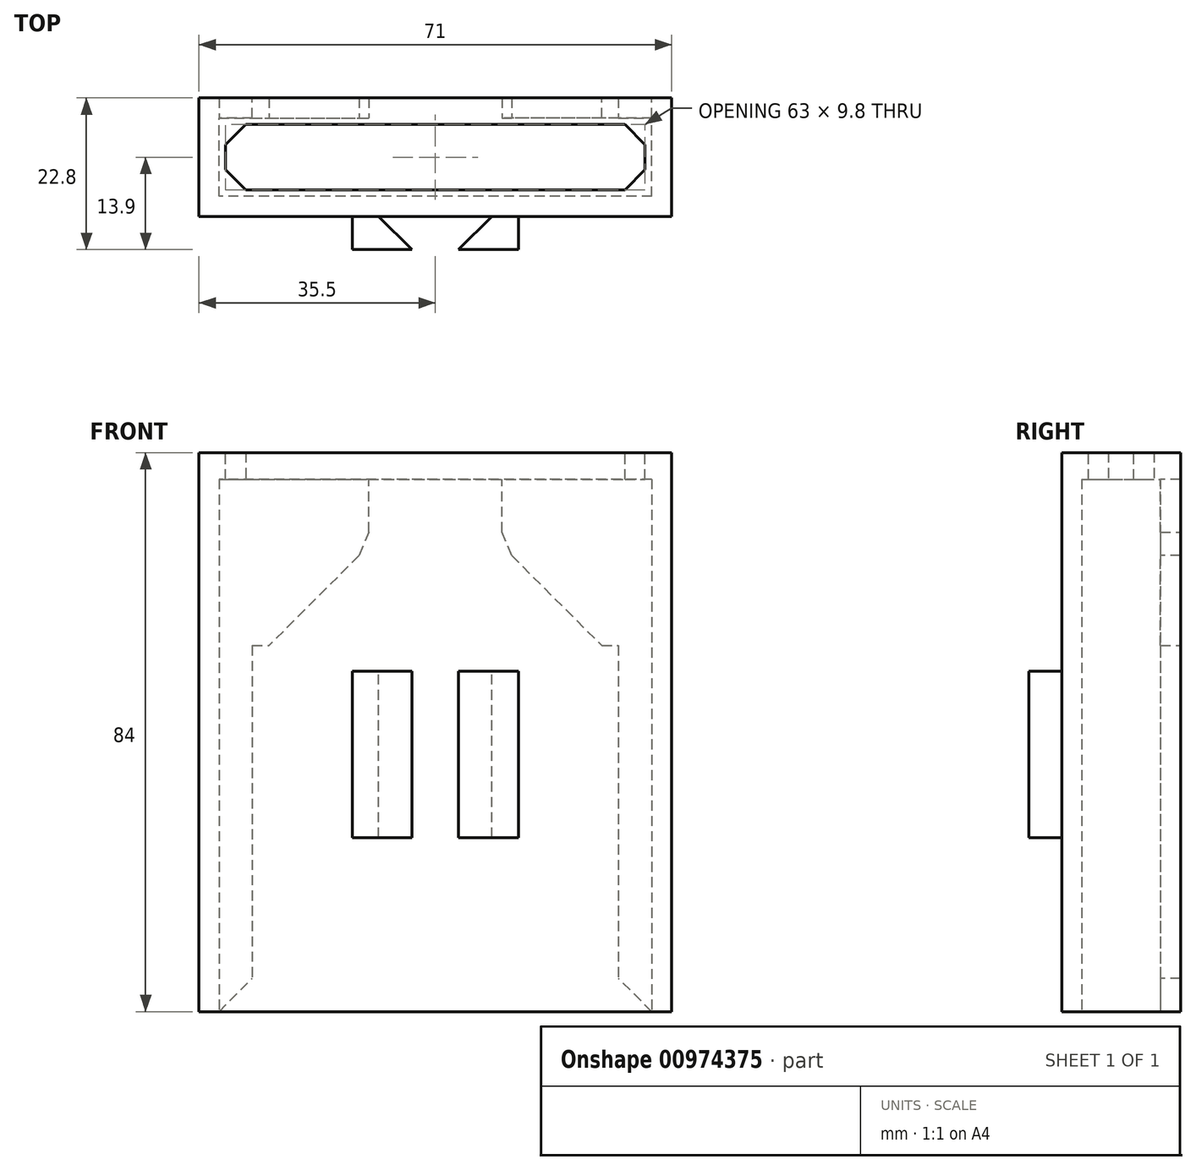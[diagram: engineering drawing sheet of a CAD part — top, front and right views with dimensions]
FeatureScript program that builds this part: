
annotation { "Feature Type Name" : "Feature", "Feature Type Description" : "" }
export const myFeature = defineFeature(function(context is Context, id is Id, definition is map)
    precondition{}
    {
        {
            var Q0;
            Q0=qCreatedBy(makeId("Top.planeOp"),FACE);
            var sketch = newSketch(context, id + "F0", { "sketchPlane" : qUnion([Q0])});
            skLineSegment(sketch, "E0.bottom", {"start": v(0, 0) * mm, "end": v(-32.5, 0) * mm});
            skLineSegment(sketch, "E0.top", {"start": v(0, 3) * mm, "end": v(-32.5, 3) * mm});
            skLineSegment(sketch, "E0.left", {"start": v(0, 0) * mm, "end": v(0, 3) * mm});
            skLineSegment(sketch, "E0.right", {"start": v(-32.5, 0) * mm, "end": v(-32.5, 3) * mm});
            skLineSegment(sketch, "E1.bottom", {"start": v(-32.5, 0) * mm, "end": v(-35.5, 0) * mm});
            skLineSegment(sketch, "E1.top", {"start": v(-32.5, 14.8) * mm, "end": v(-35.5, 14.8) * mm});
            skLineSegment(sketch, "E1.left", {"start": v(-32.5, 0) * mm, "end": v(-32.5, 14.8) * mm});
            skLineSegment(sketch, "E1.right", {"start": v(-35.5, 0) * mm, "end": v(-35.5, 14.8) * mm});
            skLineSegment(sketch, "E2.bottom", {"start": v(-35.5, 14.8) * mm, "end": v(-27.5, 14.8) * mm});
            skLineSegment(sketch, "E2.top", {"start": v(-35.5, 17.8) * mm, "end": v(-27.5, 17.8) * mm});
            skLineSegment(sketch, "E2.left", {"start": v(-35.5, 14.8) * mm, "end": v(-35.5, 17.8) * mm});
            skLineSegment(sketch, "E2.right", {"start": v(-27.5, 14.8) * mm, "end": v(-27.5, 17.8) * mm});
            skLineSegment(sketch, "E3.MirrorCS", {"start": v(0, 0) * mm, "end": v(32.5, 0) * mm});
            skLineSegment(sketch, "E4.MirrorCS", {"start": v(32.5, 0) * mm, "end": v(32.5, 14.8) * mm});
            skLineSegment(sketch, "E5.MirrorCS", {"start": v(35.5, 14.8) * mm, "end": v(35.5, 17.8) * mm});
            skLineSegment(sketch, "E6.MirrorCS", {"start": v(35.5, 0) * mm, "end": v(35.5, 14.8) * mm});
            skLineSegment(sketch, "E7.MirrorCS", {"start": v(0, 3) * mm, "end": v(32.5, 3) * mm});
            skLineSegment(sketch, "E8.MirrorCS", {"start": v(27.5, 14.8) * mm, "end": v(27.5, 17.8) * mm});
            skLineSegment(sketch, "E9.MirrorCS", {"start": v(32.5, 0) * mm, "end": v(32.5, 3) * mm});
            skLineSegment(sketch, "E10.MirrorCS", {"start": v(35.5, 14.8) * mm, "end": v(27.5, 14.8) * mm});
            skLineSegment(sketch, "E11.MirrorCS", {"start": v(32.5, 0) * mm, "end": v(35.5, 0) * mm});
            skLineSegment(sketch, "E12.MirrorCS", {"start": v(35.5, 17.8) * mm, "end": v(27.5, 17.8) * mm});
            skLineSegment(sketch, "E13.MirrorCS", {"start": v(32.5, 14.8) * mm, "end": v(35.5, 14.8) * mm});
            skSolve(sketch);
        }
        {
            var Q0;
            {var subQ5=sQuery(id+"F0.wireOp",EDGE,"E1.bottom");Q0=makeQuery(id+"F0.imprint","IMPRINT",FACE,{"disambiguationData":[TD([[makeQuery(id+"F0.imprint","IMPRINT",EDGE,{"derivedFrom":subQ5}),-1.0]])]});}
            var Q1;
            Q1=makeQuery(id+"F0.imprint","IMPRINT",FACE,{"disambiguationData":[TD([[makeQuery(id+"F0.imprint","IMPRINT",EDGE,{"derivedFrom":sQuery(id+"F0.wireOp",EDGE,"E4.MirrorCS")}),-1.0]])]});
            var Q2;
            {var subQ0=sQuery(id+"F0.wireOp",EDGE,"E0.bottom");Q2=makeQuery(id+"F0.imprint","IMPRINT",FACE,{"disambiguationData":[TD([[makeQuery(id+"F0.imprint","IMPRINT",EDGE,{"derivedFrom":subQ0}),-1.0]])]});}
            var Q3;
            Q3=makeQuery(id+"F0.imprint","IMPRINT",FACE,{"disambiguationData":[TD([[makeQuery(id+"F0.imprint","IMPRINT",EDGE,{"derivedFrom":sQuery(id+"F0.wireOp",EDGE,"E3.MirrorCS")}),1.0]])]});
            var Q4;
            Q4=makeQuery(id+"F0.imprint","IMPRINT",FACE,{"disambiguationData":[TD([[makeQuery(id+"F0.imprint","IMPRINT",EDGE,{"derivedFrom":sQuery(id+"F0.wireOp",EDGE,"E2.top")}),-1.0]])]});
            var Q5;
            Q5=makeQuery(id+"F0.imprint","IMPRINT",FACE,{"disambiguationData":[TD([[makeQuery(id+"F0.imprint","IMPRINT",EDGE,{"derivedFrom":sQuery(id+"F0.wireOp",EDGE,"E5.MirrorCS")}),1.0]])]});
            extrude(context, id + "F1", {"entities" : qUnion([Q0, Q1, Q2, Q3, Q4, Q5]), "depth" : 80 * mm, "offsetDistance" : 25 * mm});
        }
        {
            var Q0;
            Q0=makeQuery(id+"F1.opExtrude","CAP_FACE",FACE,{"disambiguationData":[OSD([sQuery(id+"F0.wireOp",EDGE,"E0.bottom"),sQuery(id+"F0.wireOp",EDGE,"E0.top"),sQuery(id+"F0.wireOp",EDGE,"E1.bottom"),sQuery(id+"F0.wireOp",EDGE,"E1.left"),sQuery(id+"F0.wireOp",EDGE,"E1.right"),sQuery(id+"F0.wireOp",EDGE,"E2.bottom"),sQuery(id+"F0.wireOp",EDGE,"E2.top"),sQuery(id+"F0.wireOp",EDGE,"E2.left"),sQuery(id+"F0.wireOp",EDGE,"E2.right"),sQuery(id+"F0.wireOp",EDGE,"E3.MirrorCS"),sQuery(id+"F0.wireOp",EDGE,"E4.MirrorCS"),sQuery(id+"F0.wireOp",EDGE,"E5.MirrorCS"),sQuery(id+"F0.wireOp",EDGE,"E6.MirrorCS"),sQuery(id+"F0.wireOp",EDGE,"E7.MirrorCS"),sQuery(id+"F0.wireOp",EDGE,"E8.MirrorCS"),sQuery(id+"F0.wireOp",EDGE,"E10.MirrorCS"),sQuery(id+"F0.wireOp",EDGE,"E11.MirrorCS"),sQuery(id+"F0.wireOp",EDGE,"E12.MirrorCS")])],"isStart":false});
            var sketch = newSketch(context, id + "F2", { "sketchPlane" : qUnion([Q0])});
            skLineSegment(sketch, "E14.bottom", {"start": v(-35.5, 17.8) * mm, "end": v(35.5, 17.8) * mm});
            skLineSegment(sketch, "E14.top", {"start": v(-35.5, 0) * mm, "end": v(35.5, 0) * mm});
            skLineSegment(sketch, "E14.left", {"start": v(-35.5, 17.8) * mm, "end": v(-35.5, 0) * mm});
            skLineSegment(sketch, "E14.right", {"start": v(35.5, 17.8) * mm, "end": v(35.5, 0) * mm});
            skSolve(sketch);
        }
        {
            var Q0;
            Q0=makeQuery(id+"F2.imprint","IMPRINT",FACE,{"disambiguationData":[TD([[makeQuery(id+"F2.imprint","IMPRINT",EDGE,{"derivedFrom":makeQuery(id+"F1.opExtrude","CAP_EDGE",EDGE,{"disambiguationData":[OSD([sQuery(id+"F0.wireOp",EDGE,"E1.left")])],"isStart":false})}),-1.0]])]});
            var Q1;
            Q1=makeQuery(id+"F2.imprint","IMPRINT",FACE,{"disambiguationData":[TD([[makeQuery(id+"F2.imprint","IMPRINT",EDGE,{"derivedFrom":sQuery(id+"F2.wireOp",EDGE,"E14.top")}),-1.0]])]});
            extrude(context, id + "F3", {"entities" : qUnion([Q0, Q1]), "operationType" : NewBodyOperationType.ADD, "depth" : 4 * mm, "offsetDistance" : 25 * mm});
        }
        {
            var Q0;
            Q0=makeQuery(id+"F3.opExtrude","CAP_FACE",FACE,{"disambiguationData":[OSD([sQuery(id+"F2.wireOp",EDGE,"E14.bottom"),sQuery(id+"F2.wireOp",EDGE,"E14.top"),sQuery(id+"F2.wireOp",EDGE,"E14.left"),sQuery(id+"F2.wireOp",EDGE,"E14.right")])],"isStart":true});
            var sketch = newSketch(context, id + "F4", { "sketchPlane" : qUnion([Q0])});
            skLineSegment(sketch, "E15.bottom", {"start": v(-27.5, -17.8) * mm, "end": v(-10, -17.8) * mm});
            skLineSegment(sketch, "E15.top", {"start": v(-27.5, -14.8) * mm, "end": v(-10, -14.8) * mm});
            skLineSegment(sketch, "E15.left", {"start": v(-27.5, -17.8) * mm, "end": v(-27.5, -14.8) * mm});
            skLineSegment(sketch, "E15.right", {"start": v(-10, -17.8) * mm, "end": v(-10, -14.8) * mm});
            skPoint(sketch, "E16.MirrorCS.end.orphan", {"position": v(-10, -11.8) * mm});
            skPoint(sketch, "E16.MirrorCS.start.orphan", {"position": v(-27.5, -11.8) * mm});
            skPoint(sketch, "E17.MirrorCS.end.orphan", {"position": v(-10, -14.8) * mm});
            skPoint(sketch, "E18.MirrorCS.end.orphan", {"position": v(-27.5, -14.8) * mm});
            skLineSegment(sketch, "E19.MirrorCS", {"start": v(27.5, -17.8) * mm, "end": v(10, -17.8) * mm});
            skLineSegment(sketch, "E20.MirrorCS", {"start": v(10, -17.8) * mm, "end": v(10, -14.8) * mm});
            skLineSegment(sketch, "E21.MirrorCS", {"start": v(27.5, -14.8) * mm, "end": v(10, -14.8) * mm});
            skLineSegment(sketch, "E22.MirrorCS", {"start": v(27.5, -17.8) * mm, "end": v(27.5, -14.8) * mm});
            skSolve(sketch);
        }
        {
            var Q0;
            Q0=makeQuery(id+"F4.imprint","IMPRINT",FACE,{"disambiguationData":[TD([[makeQuery(id+"F4.imprint","IMPRINT",EDGE,{"derivedFrom":sQuery(id+"F4.wireOp",EDGE,"E15.bottom")}),1.0]])]});
            var Q1;
            Q1=makeQuery(id+"F4.imprint","IMPRINT",FACE,{"disambiguationData":[TD([[makeQuery(id+"F4.imprint","IMPRINT",EDGE,{"derivedFrom":sQuery(id+"F4.wireOp",EDGE,"E19.MirrorCS")}),1.0]])]});
            extrude(context, id + "F5", {"entities" : qUnion([Q0, Q1]), "operationType" : NewBodyOperationType.ADD, "depth" : 25 * mm, "offsetDistance" : 25 * mm});
        }
        {
            var Q0;
            Q0=makeQuery(id+"F5.opExtrude","CAP_EDGE",EDGE,{"disambiguationData":[OSD([sQuery(id+"F4.wireOp",EDGE,"E15.right")])],"isStart":false});
            var Q1;
            Q1=makeQuery(id+"F5.opExtrude","CAP_EDGE",EDGE,{"disambiguationData":[OSD([sQuery(id+"F4.wireOp",EDGE,"E20.MirrorCS")])],"isStart":false});
            chamfer(context, id + "F6", {"entities" : qUnion([Q0, Q1]), "width" : 15 * mm, "tangentPropagation" : true});
        }
        {
            var Q0;
            {var subQ0=sQuery(id+"F4.wireOp",EDGE,"E15.right");Q0=makeQuery(id+"F6.opChamfer","BLEND_EDGE",EDGE,{"blendedFrom":[makeQuery(id+"F5.opExtrude","CAP_EDGE",EDGE,{"disambiguationData":[OSD([subQ0])],"isStart":false}),makeQuery(id+"F5.opExtrude","SWEPT_FACE",FACE,{"disambiguationData":[OSD([subQ0])]})],"blendedInto":[makeQuery(id+"F5.opExtrude","SWEPT_FACE",FACE,{"disambiguationData":[OSD([subQ0])]})]});}
            var Q1;
            {var subQ0=sQuery(id+"F4.wireOp",EDGE,"E20.MirrorCS");Q1=makeQuery(id+"F6.opChamfer","BLEND_EDGE",EDGE,{"blendedFrom":[makeQuery(id+"F5.opExtrude","CAP_EDGE",EDGE,{"disambiguationData":[OSD([subQ0])],"isStart":false}),makeQuery(id+"F5.opExtrude","SWEPT_FACE",FACE,{"disambiguationData":[OSD([subQ0])]})],"blendedInto":[makeQuery(id+"F5.opExtrude","SWEPT_FACE",FACE,{"disambiguationData":[OSD([subQ0])]})]});}
            chamfer(context, id + "F7", {"entities" : qUnion([Q0, Q1]), "width" : 5 * mm, "tangentPropagation" : true});
        }
        {
            var Q0;
            Q0=makeQuery(id+"F3.opExtrude","CAP_FACE",FACE,{"disambiguationData":[OSD([sQuery(id+"F2.wireOp",EDGE,"E14.bottom"),sQuery(id+"F2.wireOp",EDGE,"E14.top"),sQuery(id+"F2.wireOp",EDGE,"E14.left"),sQuery(id+"F2.wireOp",EDGE,"E14.right")])],"isStart":false});
            var sketch = newSketch(context, id + "F8", { "sketchPlane" : qUnion([Q0])});
            skLineSegment(sketch, "E23.0", {"start": v(-31.5, 13.8) * mm, "end": v(31.5, 13.8) * mm});
            skLineSegment(sketch, "E23.1", {"start": v(-31.5, 4) * mm, "end": v(-31.5, 13.8) * mm});
            skLineSegment(sketch, "E23.2", {"start": v(31.5, 4) * mm, "end": v(-31.5, 4) * mm});
            skLineSegment(sketch, "E23.3", {"start": v(31.5, 4) * mm, "end": v(31.5, 13.8) * mm});
            skSolve(sketch);
        }
        {
            var Q0;
            Q0=makeQuery(id+"F8.imprint","IMPRINT",FACE,{"disambiguationData":[TD([[makeQuery(id+"F8.imprint","IMPRINT",EDGE,{"derivedFrom":sQuery(id+"F8.wireOp",EDGE,"E23.0")}),-1.0]])]});
            extrude(context, id + "F9", {"entities" : qUnion([Q0]), "operationType" : NewBodyOperationType.REMOVE, "oppositeDirection" : true, "depth" : 4 * mm, "offsetDistance" : 25 * mm});
        }
        {
            var Q0;
            Q0=makeQuery(id+"F9.boolean.opBoolean","COPY",EDGE,{"derivedFrom":makeQuery(id+"F9.opExtrude","SWEPT_EDGE",EDGE,{"disambiguationData":[OSD([sQuery(id+"F8.wireOp",EDGE,"E23.0"),sQuery(id+"F8.wireOp",EDGE,"E23.1")])]})});
            var Q1;
            Q1=makeQuery(id+"F9.boolean.opBoolean","COPY",EDGE,{"derivedFrom":makeQuery(id+"F9.opExtrude","SWEPT_EDGE",EDGE,{"disambiguationData":[OSD([sQuery(id+"F8.wireOp",EDGE,"E23.1"),sQuery(id+"F8.wireOp",EDGE,"E23.2")])]})});
            var Q2;
            Q2=makeQuery(id+"F9.boolean.opBoolean","COPY",EDGE,{"derivedFrom":makeQuery(id+"F9.opExtrude","SWEPT_EDGE",EDGE,{"disambiguationData":[OSD([sQuery(id+"F8.wireOp",EDGE,"E23.2"),sQuery(id+"F8.wireOp",EDGE,"E23.3")])]})});
            var Q3;
            Q3=makeQuery(id+"F9.boolean.opBoolean","COPY",EDGE,{"derivedFrom":makeQuery(id+"F9.opExtrude","SWEPT_EDGE",EDGE,{"disambiguationData":[OSD([sQuery(id+"F8.wireOp",EDGE,"E23.0"),sQuery(id+"F8.wireOp",EDGE,"E23.3")])]})});
            var Q4;
            Q4=makeQuery(id+"F5.opExtrude","CAP_EDGE",EDGE,{"disambiguationData":[OSD([sQuery(id+"F4.wireOp",EDGE,"E20.MirrorCS")])],"isStart":true});
            var Q5;
            Q5=makeQuery(id+"F5.opExtrude","CAP_EDGE",EDGE,{"disambiguationData":[OSD([sQuery(id+"F4.wireOp",EDGE,"E15.right")])],"isStart":true});
            chamfer(context, id + "F10", {"entities" : qUnion([Q0, Q1, Q2, Q3, Q4, Q5]), "width" : 3 * mm, "tangentPropagation" : true});
        }
        {
            var Q0;
            Q0=makeQuery(id+"F1.opExtrude","CAP_EDGE",EDGE,{"disambiguationData":[OSD([sQuery(id+"F0.wireOp",EDGE,"E2.right")])],"isStart":true});
            var Q1;
            Q1=makeQuery(id+"F1.opExtrude","CAP_EDGE",EDGE,{"disambiguationData":[OSD([sQuery(id+"F0.wireOp",EDGE,"E8.MirrorCS")])],"isStart":true});
            chamfer(context, id + "F11", {"entities" : qUnion([Q0, Q1]), "width" : 5 * mm, "tangentPropagation" : true});
        }
        {
            var Q0;
            Q0=makeQuery(id+"F3.boolean.opBoolean","MERGE",FACE,{"derivedFrom":[makeQuery(id+"F1.opExtrude","SWEPT_FACE",FACE,{"disambiguationData":[OSD([sQuery(id+"F0.wireOp",EDGE,"E0.bottom"),sQuery(id+"F0.wireOp",EDGE,"E1.bottom"),sQuery(id+"F0.wireOp",EDGE,"E3.MirrorCS"),sQuery(id+"F0.wireOp",EDGE,"E11.MirrorCS")])]}),makeQuery(id+"F3.opExtrude","SWEPT_FACE",FACE,{"disambiguationData":[OSD([sQuery(id+"F2.wireOp",EDGE,"E14.top")])]})]});
            var sketch = newSketch(context, id + "F12", { "sketchPlane" : qUnion([Q0])});
            skLineSegment(sketch, "E24.bottom", {"start": v(-35.5, 84) * mm, "end": v(-30.5, 84) * mm});
            skLineSegment(sketch, "E24.top", {"start": v(-35.5, 79) * mm, "end": v(-30.5, 79) * mm});
            skLineSegment(sketch, "E24.left", {"start": v(-35.5, 84) * mm, "end": v(-35.5, 79) * mm});
            skLineSegment(sketch, "E24.right", {"start": v(-30.5, 84) * mm, "end": v(-30.5, 79) * mm});
            skLineSegment(sketch, "E25.MirrorCS", {"start": v(30.5, 84) * mm, "end": v(30.5, 79) * mm});
            skLineSegment(sketch, "E26.MirrorCS", {"start": v(35.5, 79) * mm, "end": v(30.5, 79) * mm});
            skLineSegment(sketch, "E27.MirrorCS", {"start": v(35.5, 84) * mm, "end": v(35.5, 79) * mm});
            skLineSegment(sketch, "E28.MirrorCS", {"start": v(35.5, 84) * mm, "end": v(30.5, 84) * mm});
            skLineSegment(sketch, "E29.bottom", {"start": v(12.5, 51.17) * mm, "end": v(-12.5, 51.17) * mm});
            skLineSegment(sketch, "E29.top", {"start": v(12.5, 26.17) * mm, "end": v(-12.5, 26.17) * mm});
            skLineSegment(sketch, "E29.left", {"start": v(12.5, 51.17) * mm, "end": v(12.5, 26.17) * mm});
            skLineSegment(sketch, "E29.right", {"start": v(-12.5, 51.17) * mm, "end": v(-12.5, 26.17) * mm});
            skPoint(sketch, "E29.middle", {"position": v(0, 38.67) * mm});
            skSolve(sketch);
        }
        {
            var Q0;
            Q0=makeQuery(id+"F12.imprint","IMPRINT",FACE,{"disambiguationData":[TD([[makeQuery(id+"F12.imprint","IMPRINT",EDGE,{"derivedFrom":sQuery(id+"F12.wireOp",EDGE,"E29.bottom")}),1.0]])]});
            extrude(context, id + "F13", {"entities" : qUnion([Q0]), "operationType" : NewBodyOperationType.ADD, "depth" : 5 * mm, "offsetDistance" : 25 * mm});
        }
        {
            var Q0;
            Q0=makeQuery(id+"F13.opExtrude","SWEPT_FACE",FACE,{"disambiguationData":[OSD([sQuery(id+"F12.wireOp",EDGE,"E29.bottom")])]});
            var sketch = newSketch(context, id + "F14", { "sketchPlane" : qUnion([Q0])});
            skLineSegment(sketch, "E30", {"start": v(-8.5, 0) * mm, "end": v(-3.5, -5) * mm});
            skLineSegment(sketch, "E31", {"start": v(-8.5, 0) * mm, "end": v(-12.5, 0) * mm});
            skLineSegment(sketch, "E32", {"start": v(-12.5, 0) * mm, "end": v(-12.5, -5) * mm});
            skLineSegment(sketch, "E33", {"start": v(-12.5, -5) * mm, "end": v(-3.5, -5) * mm});
            skLineSegment(sketch, "E34.MirrorCS", {"start": v(12.5, -5) * mm, "end": v(3.5, -5) * mm});
            skLineSegment(sketch, "E35.MirrorCS", {"start": v(8.5, 0) * mm, "end": v(3.5, -5) * mm});
            skLineSegment(sketch, "E36.MirrorCS", {"start": v(8.5, 0) * mm, "end": v(12.5, 0) * mm});
            skLineSegment(sketch, "E37.MirrorCS", {"start": v(12.5, 0) * mm, "end": v(12.5, -5) * mm});
            skSolve(sketch);
        }
        {
            var Q0;
            {var subQ0=sQuery(id+"F14.wireOp",EDGE,"E30");Q0=makeQuery(id+"F14.imprint","IMPRINT",FACE,{"disambiguationData":[TD([[makeQuery(id+"F14.imprint","IMPRINT",EDGE,{"derivedFrom":subQ0}),1.0]])]});}
            extrude(context, id + "F15", {"entities" : qUnion([Q0]), "operationType" : NewBodyOperationType.REMOVE, "oppositeDirection" : true, "depth" : 25 * mm, "offsetDistance" : 25 * mm});
        }
    });
